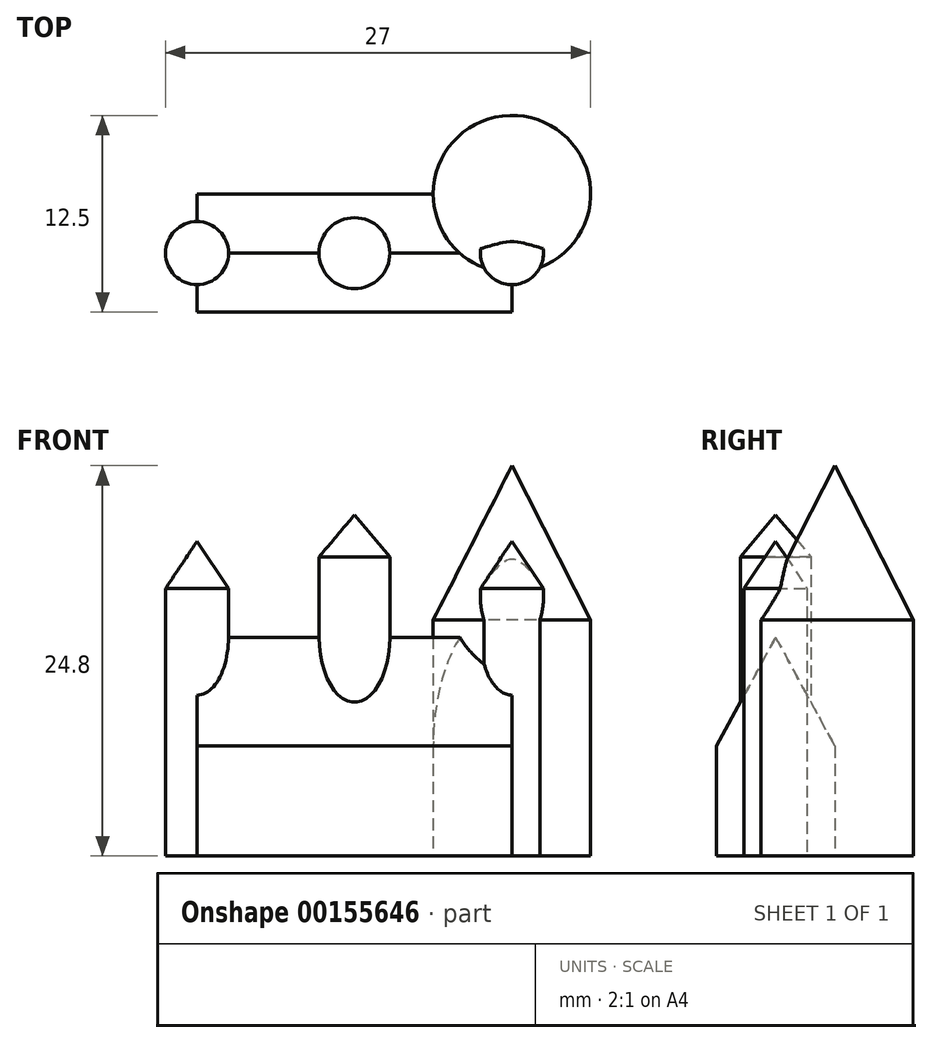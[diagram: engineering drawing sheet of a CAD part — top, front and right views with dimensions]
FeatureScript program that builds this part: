
annotation { "Feature Type Name" : "Feature", "Feature Type Description" : "" }
export const myFeature = defineFeature(function(context is Context, id is Id, definition is map)
    precondition{}
    {
        {
            var Q0;
            Q0=qCreatedBy(makeId("Top.planeOp"),FACE);
            var sketch = newSketch(context, id + "F0", { "sketchPlane" : qUnion([Q0])});
            skCircle(sketch, "E0", {"center": v(0, 0) * mm, "radius": 5 * mm});
            skLineSegment(sketch, "E1.bottom", {"start": v(0, 0) * mm, "end": v(-20, 0) * mm});
            skLineSegment(sketch, "E1.top", {"start": v(0, -7.5) * mm, "end": v(-20, -7.5) * mm});
            skLineSegment(sketch, "E1.left", {"start": v(0, 0) * mm, "end": v(0, -7.5) * mm});
            skLineSegment(sketch, "E1.right", {"start": v(-20, 0) * mm, "end": v(-20, -7.5) * mm});
            skSolve(sketch);
        }
        {
            var Q0;
            {var subQ0=sQuery(id+"F0.wireOp",EDGE,"E1.bottom");var subQ1=sQuery(id+"F0.wireOp",EDGE,"E0");var subQ2=makeQuery(id+"F0.imprint","INTERSECT",VERTEX,{"derivedFrom":[subQ1,subQ0]});Q0=makeQuery(id+"F0.imprint","IMPRINT",FACE,{"disambiguationData":[TD([[makeQuery(id+"F0.imprint","IMPRINT",EDGE,{"disambiguationData":[TD([[subQ2,1.0]])],"derivedFrom":subQ1}),1.0]])]});}
            var Q1;
            {var subQ0=sQuery(id+"F0.wireOp",EDGE,"E1.bottom");var subQ1=sQuery(id+"F0.wireOp",EDGE,"E0");var subQ2=makeQuery(id+"F0.imprint","INTERSECT",VERTEX,{"derivedFrom":[subQ1,subQ0]});Q1=makeQuery(id+"F0.imprint","IMPRINT",FACE,{"disambiguationData":[TD([[makeQuery(id+"F0.imprint","IMPRINT",EDGE,{"disambiguationData":[TD([[subQ2,-1.0]])],"derivedFrom":subQ1}),1.0]])]});}
            extrude(context, id + "F1", {"entities" : qUnion([Q0, Q1]), "depth" : 15 * mm});
        }
        {
            var Q0;
            {var subQ1=sQuery(id+"F0.wireOp",EDGE,"E1.top");Q0=makeQuery(id+"F0.imprint","IMPRINT",FACE,{"disambiguationData":[TD([[makeQuery(id+"F0.imprint","IMPRINT",EDGE,{"derivedFrom":subQ1}),-1.0]])]});}
            extrude(context, id + "F2", {"entities" : qUnion([Q0]), "operationType" : NewBodyOperationType.ADD, "depth" : 7 * mm});
        }
        {
            var Q0;
            Q0=qCreatedBy(makeId("Front.planeOp"),FACE);
            var sketch = newSketch(context, id + "F3", { "sketchPlane" : qUnion([Q0])});
            skLineSegment(sketch, "E2.0", {"start": v(-5, 15) * mm, "end": v(5, 15) * mm});
            skLineSegment(sketch, "E3", {"start": v(-5, 15) * mm, "end": v(0, 24.8) * mm});
            skLineSegment(sketch, "E4", {"start": v(0, 24.8) * mm, "end": v(0, 15) * mm});
            skSolve(sketch);
        }
        {
            var Q0;
            {var subQ0=sQuery(id+"F3.wireOp",EDGE,"E3");Q0=makeQuery(id+"F3.imprint","IMPRINT",FACE,{"disambiguationData":[TD([[makeQuery(id+"F3.imprint","IMPRINT",EDGE,{"derivedFrom":subQ0}),-1.0]])]});}
            var Q1;
            Q1=sQuery(id+"F3.wireOp",EDGE,"E4");
            revolve(context, id + "F4", {"operationType" : NewBodyOperationType.ADD, "entities" : qUnion([Q0]), "axis" : qUnion([Q1]), "revolveType" : RevolveType.FULL});
        }
        {
            var Q0;
            Q0=makeQuery(id+"F2.opExtrude","CAP_FACE",FACE,{"disambiguationData":[OSD([sQuery(id+"F0.wireOp",EDGE,"E0"),sQuery(id+"F0.wireOp",EDGE,"E1.bottom"),sQuery(id+"F0.wireOp",EDGE,"E1.top"),sQuery(id+"F0.wireOp",EDGE,"E1.left"),sQuery(id+"F0.wireOp",EDGE,"E1.right")])],"isStart":false});
            var sketch = newSketch(context, id + "F5", { "sketchPlane" : qUnion([Q0])});
            skCircle(sketch, "E5", {"center": v(-20, -3.75) * mm, "radius": 2 * mm});
            skLineSegment(sketch, "E6", {"start": v(-20, -3.75) * mm, "end": v(0, -3.75) * mm, "construction": true});
            skCircle(sketch, "E7", {"center": v(0, -3.75) * mm, "radius": 2 * mm});
            skCircle(sketch, "E8", {"center": v(-10, -3.75) * mm, "radius": 2.25 * mm});
            skSolve(sketch);
        }
        {
            var Q0;
            Q0=makeQuery(id+"F5.imprint","IMPRINT",FACE,{"disambiguationData":[TD([[makeQuery(id+"F5.imprint","IMPRINT",EDGE,{"derivedFrom":sQuery(id+"F5.wireOp",EDGE,"E7")}),1.0]])]});
            var Q1;
            {var subQ0=sQuery(id+"F5.wireOp",EDGE,"E5");var subQ1=makeQuery(id+"F2.opExtrude","CAP_EDGE",EDGE,{"disambiguationData":[OSD([sQuery(id+"F0.wireOp",EDGE,"E1.right")])],"isStart":false});var subQ2=makeQuery(id+"F5.imprint","INTERSECT",VERTEX,{"disambiguationData":[OD(0.0)],"derivedFrom":[subQ1,subQ0]});Q1=makeQuery(id+"F5.imprint","IMPRINT",FACE,{"disambiguationData":[TD([[makeQuery(id+"F5.imprint","IMPRINT",EDGE,{"disambiguationData":[TD([[subQ2,-1.0]])],"derivedFrom":subQ0}),1.0]])]});}
            var Q2;
            {var subQ0=sQuery(id+"F5.wireOp",EDGE,"E5");var subQ1=makeQuery(id+"F2.opExtrude","CAP_EDGE",EDGE,{"disambiguationData":[OSD([sQuery(id+"F0.wireOp",EDGE,"E1.right")])],"isStart":false});var subQ2=makeQuery(id+"F5.imprint","INTERSECT",VERTEX,{"disambiguationData":[OD(0.0)],"derivedFrom":[subQ1,subQ0]});Q2=makeQuery(id+"F5.imprint","IMPRINT",FACE,{"disambiguationData":[TD([[makeQuery(id+"F5.imprint","IMPRINT",EDGE,{"disambiguationData":[TD([[subQ2,1.0]])],"derivedFrom":subQ0}),1.0]])]});}
            var Q3;
            {var subQ0=sQuery(id+"F0.wireOp",EDGE,"E0");Q3=makeQuery(id+"F2.boolean.opBoolean","MERGE",FACE,{"derivedFrom":[makeQuery(id+"F1.opExtrude","CAP_FACE",FACE,{"disambiguationData":[OSD([subQ0])],"isStart":true}),makeQuery(id+"F2.opExtrude","CAP_FACE",FACE,{"disambiguationData":[OSD([subQ0,sQuery(id+"F0.wireOp",EDGE,"E1.bottom"),sQuery(id+"F0.wireOp",EDGE,"E1.top"),sQuery(id+"F0.wireOp",EDGE,"E1.left"),sQuery(id+"F0.wireOp",EDGE,"E1.right")])],"isStart":true})]});}
            extrude(context, id + "F6", {"entities" : qUnion([Q0, Q1, Q2]), "operationType" : NewBodyOperationType.ADD, "depth" : 10 * mm, "hasSecondDirection" : true, "secondDirectionBound" : BoundingType.UP_TO_SURFACE, "secondDirectionOppositeDirection" : true, "secondDirectionBoundEntityFace" : qUnion([Q3]), "secondDirectionDepth" : 25 * mm});
        }
        {
            var Q0;
            Q0=makeQuery(id+"F5.imprint","IMPRINT",FACE,{"disambiguationData":[TD([[makeQuery(id+"F5.imprint","IMPRINT",EDGE,{"derivedFrom":sQuery(id+"F5.wireOp",EDGE,"E8")}),1.0]])]});
            extrude(context, id + "F7", {"entities" : qUnion([Q0]), "operationType" : NewBodyOperationType.ADD, "depth" : 12 * mm});
        }
        {
            var Q0;
            Q0=makeQuery(id+"F2.opExtrude","SWEPT_FACE",FACE,{"disambiguationData":[OSD([sQuery(id+"F0.wireOp",EDGE,"E1.right")])]});
            var sketch = newSketch(context, id + "F8", { "sketchPlane" : qUnion([Q0])});
            skLineSegment(sketch, "E9", {"start": v(0, 7) * mm, "end": v(3.75, 13.9) * mm});
            skLineSegment(sketch, "E10", {"start": v(3.75, 13.9) * mm, "end": v(7.5, 7) * mm});
            skLineSegment(sketch, "E11", {"start": v(0, 7) * mm, "end": v(7.5, 7) * mm});
            skLineSegment(sketch, "E12", {"start": v(3.75, 7) * mm, "end": v(3.75, 15.9) * mm, "construction": true});
            skSolve(sketch);
        }
        {
            var Q0;
            Q0=makeQuery(id+"F8.imprint","IMPRINT",FACE,{"disambiguationData":[TD([[makeQuery(id+"F8.imprint","IMPRINT",EDGE,{"derivedFrom":sQuery(id+"F8.wireOp",EDGE,"E9")}),-1.0]])]});
            var Q1;
            Q1=makeQuery(id+"F2.opExtrude","SWEPT_FACE",FACE,{"disambiguationData":[OSD([sQuery(id+"F0.wireOp",EDGE,"E1.left")])]});
            extrude(context, id + "F9", {"entities" : qUnion([Q0]), "operationType" : NewBodyOperationType.ADD, "endBound" : BoundingType.UP_TO_SURFACE, "oppositeDirection" : true, "endBoundEntityFace" : qUnion([Q1]), "depth" : 25 * mm});
        }
        {
            var Q0;
            {var subQ0=sQuery(id+"F8.wireOp",EDGE,"E9");var subQ1=sQuery(id+"F8.wireOp",EDGE,"E10");Q0=makeQuery(id+"F9.boolean.opBoolean","SPLIT",EDGE,{"disambiguationData":[TD([makeQuery(id+"F6.opExtrude","SWEPT_FACE",FACE,{"disambiguationData":[OSD([sQuery(id+"F5.wireOp",EDGE,"E5")])]})])],"derivedFrom":makeQuery(id+"F9.opExtrude","SWEPT_EDGE",EDGE,{"disambiguationData":[OSD([subQ0,subQ1])]})});}
            cPlane(context, id + "F10", {"entities" : qUnion([Q0]), "cplaneType" : CPlaneType.LINE_ANGLE, "offset" : 25 * mm, "angle" : 0 * degree, "width" : 150 * mm, "height" : 150 * mm});
        }
        {
            var Q0;
            Q0=qCreatedBy(id+"F10.planeOp",FACE);
            var sketch = newSketch(context, id + "F11", { "sketchPlane" : qUnion([Q0])});
            skLineSegment(sketch, "E13.0", {"start": v(-22, 17) * mm, "end": v(-18, 17) * mm});
            skLineSegment(sketch, "E14.0", {"start": v(-12.25, 19) * mm, "end": v(-7.75, 19) * mm});
            skLineSegment(sketch, "E15.0", {"start": v(-2, 17) * mm, "end": v(2, 17) * mm});
            skLineSegment(sketch, "E16", {"start": v(-20, 17) * mm, "end": v(-20, 20.54) * mm});
            skLineSegment(sketch, "E17", {"start": v(-10, 19) * mm, "end": v(-10, 24.12) * mm});
            skLineSegment(sketch, "E18", {"start": v(0, 17) * mm, "end": v(0, 21.51) * mm});
            skPoint(sketch, "E18.endSnap0", {"position": v(0, 17) * mm});
            skLineSegment(sketch, "E19", {"start": v(-22, 17) * mm, "end": v(-20, 20) * mm});
            skLineSegment(sketch, "E20", {"start": v(-2, 17) * mm, "end": v(0, 20) * mm});
            skLineSegment(sketch, "E21", {"start": v(-12.25, 19) * mm, "end": v(-10, 21.68) * mm});
            skSolve(sketch);
        }
        {
            var Q0;
            {var subQ0=sQuery(id+"F11.wireOp",EDGE,"E19");Q0=makeQuery(id+"F11.imprint","IMPRINT",FACE,{"disambiguationData":[TD([[makeQuery(id+"F11.imprint","IMPRINT",EDGE,{"derivedFrom":subQ0}),-1.0]])]});}
            var Q1;
            Q1=sQuery(id+"F11.wireOp",EDGE,"E16");
            revolve(context, id + "F12", {"operationType" : NewBodyOperationType.ADD, "entities" : qUnion([Q0]), "axis" : qUnion([Q1]), "revolveType" : RevolveType.FULL});
        }
        {
            var Q0;
            {var subQ0=sQuery(id+"F11.wireOp",EDGE,"E21");Q0=makeQuery(id+"F11.imprint","IMPRINT",FACE,{"disambiguationData":[TD([[makeQuery(id+"F11.imprint","IMPRINT",EDGE,{"derivedFrom":subQ0}),-1.0]])]});}
            var Q1;
            Q1=sQuery(id+"F11.wireOp",EDGE,"E17");
            revolve(context, id + "F13", {"operationType" : NewBodyOperationType.ADD, "entities" : qUnion([Q0]), "axis" : qUnion([Q1]), "revolveType" : RevolveType.FULL});
        }
        {
            var Q0;
            {var subQ0=sQuery(id+"F11.wireOp",EDGE,"E20");Q0=makeQuery(id+"F11.imprint","IMPRINT",FACE,{"disambiguationData":[TD([[makeQuery(id+"F11.imprint","IMPRINT",EDGE,{"derivedFrom":subQ0}),-1.0]])]});}
            var Q1;
            Q1=sQuery(id+"F11.wireOp",EDGE,"E18");
            revolve(context, id + "F14", {"operationType" : NewBodyOperationType.ADD, "entities" : qUnion([Q0]), "axis" : qUnion([Q1]), "revolveType" : RevolveType.FULL});
        }
    });
